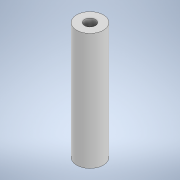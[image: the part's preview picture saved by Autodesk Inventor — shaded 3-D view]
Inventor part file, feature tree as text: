
AUTODESK INVENTOR PART (.ipt)
format: ipt  version: 2020 (Build 240168000, 168)  size: 95,744 bytes
history: native  units: mm
features: other x1, extrude x1, sketch x1
ambient origin geometry x8: Origin, YZ Plane, XZ Plane, XY Plane, X Axis, Y Axis, Z Axis, Center Point
bodies: Body1 (feature_tree)
feature tree (3):
  other  "Твердое тело1"
  extrude  "Выдавливание1"  Depth=3.3mm
  sketch  "Эскиз1"
